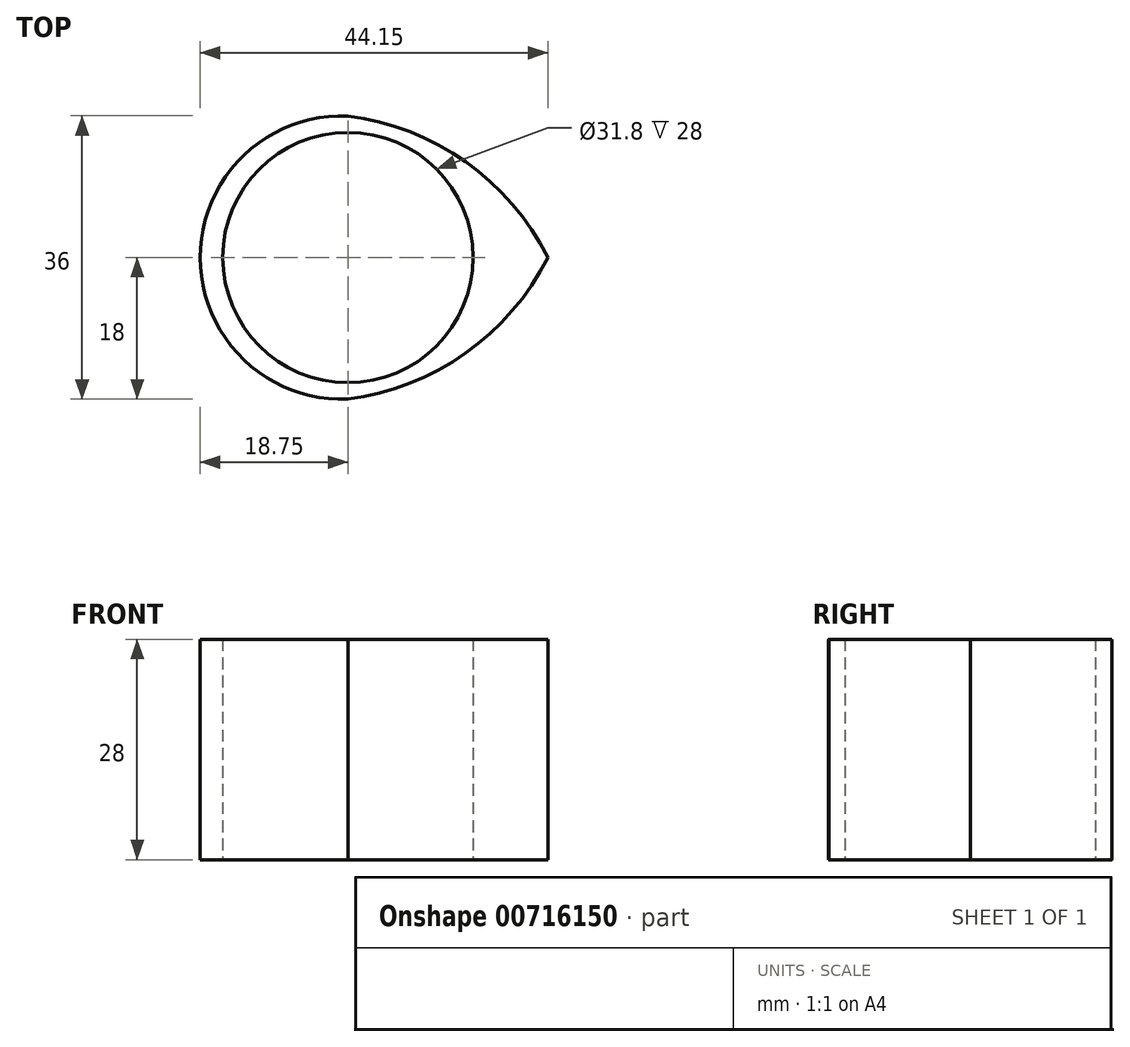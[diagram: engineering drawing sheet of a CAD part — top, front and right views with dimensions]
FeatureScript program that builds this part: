
annotation { "Feature Type Name" : "Feature", "Feature Type Description" : "" }
export const myFeature = defineFeature(function(context is Context, id is Id, definition is map)
    precondition{}
    {
        {
            var Q0;
            Q0=qCreatedBy(makeId("Top.planeOp"),FACE);
            var sketch = newSketch(context, id + "F0", { "sketchPlane" : qUnion([Q0])});
            skCircle(sketch, "E0", {"center": v(0, 0) * mm, "radius": 15.9 * mm});
            skPoint(sketch, "E1", {"position": v(0, -17.98) * mm});
            skPoint(sketch, "E2", {"position": v(0, 17.98) * mm});
            skArc(sketch, "E3", {"start": v(0, 17.98) * mm, "mid": v(-18.75, 0) * mm, "end": v(0, -17.98) * mm});
            skPoint(sketch, "E4", {"position": v(15.9, 0) * mm});
            skPoint(sketch, "E5", {"position": v(25.4, 0) * mm});
            skArc(sketch, "E6", {"start": v(0, -17.98) * mm, "mid": v(14.94, -12.16) * mm, "end": v(25.4, 0) * mm});
            skArc(sketch, "E7.MirrorCS", {"start": v(0, 17.98) * mm, "mid": v(14.94, 12.16) * mm, "end": v(25.4, 0) * mm});
            skLineSegment(sketch, "E8", {"start": v(15.9, 0) * mm, "end": v(25.4, 0) * mm, "construction": true});
            skPoint(sketch, "E9", {"position": v(20.65, 0) * mm});
            skSolve(sketch);
        }
        {
            var Q0;
            Q0=makeQuery(id+"F0.imprint","IMPRINT",FACE,{"disambiguationData":[TD([[makeQuery(id+"F0.imprint","IMPRINT",EDGE,{"derivedFrom":sQuery(id+"F0.wireOp",EDGE,"E0")}),-1.0]])]});
            extrude(context, id + "F1", {"entities" : qUnion([Q0]), "depth" : 28 * mm, "offsetDistance" : 25 * mm});
        }
    });
